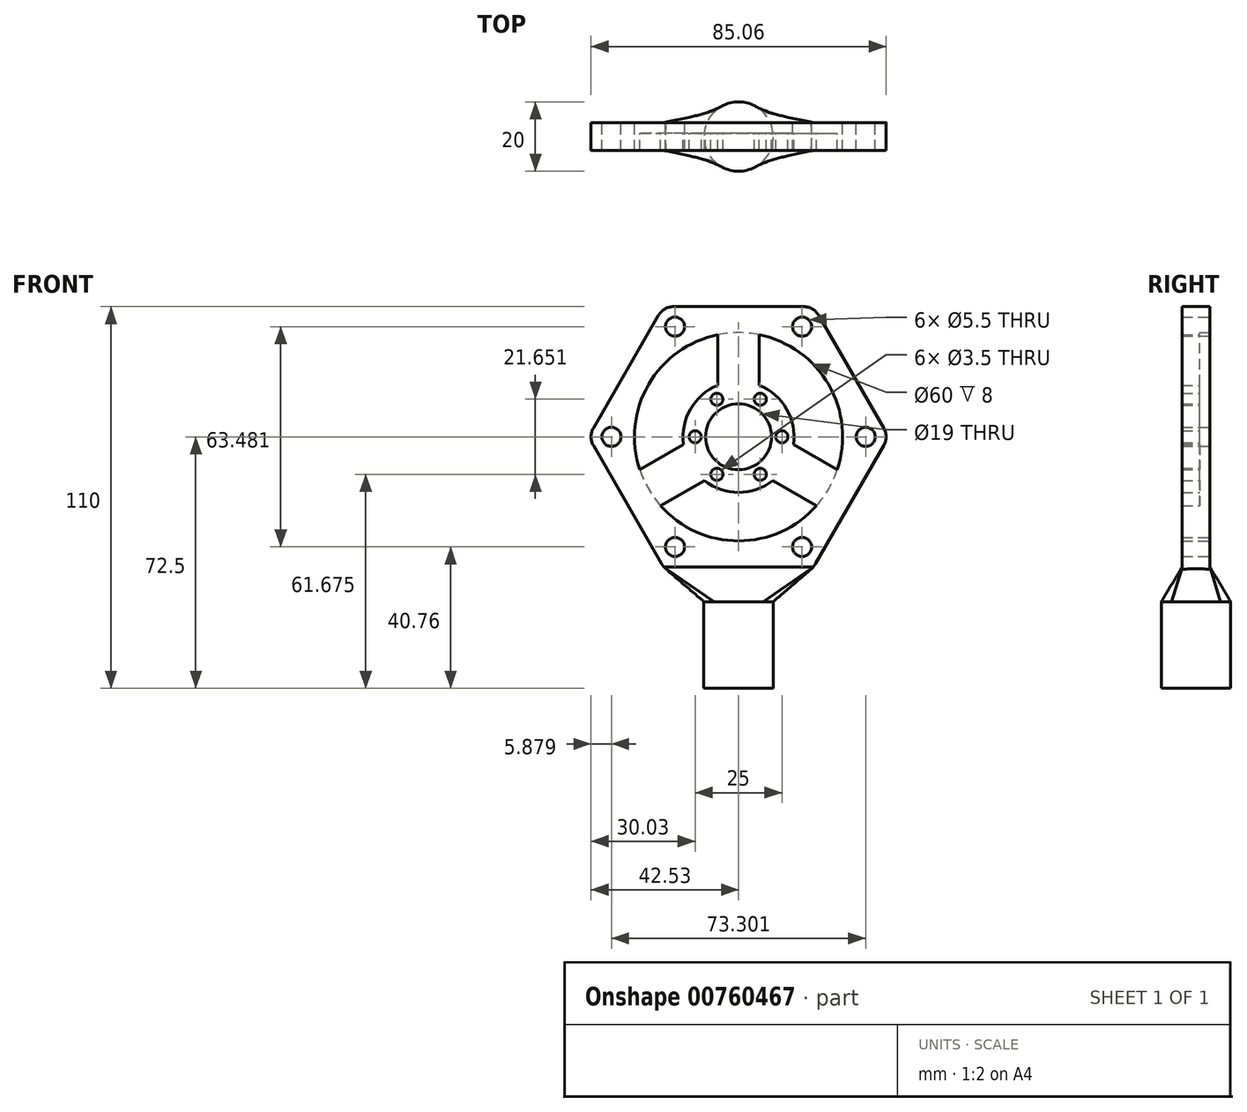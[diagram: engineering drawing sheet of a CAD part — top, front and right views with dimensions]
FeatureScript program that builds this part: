
annotation { "Feature Type Name" : "Feature", "Feature Type Description" : "" }
export const myFeature = defineFeature(function(context is Context, id is Id, definition is map)
    precondition{}
    {
        {
            var Q0;
            Q0=qCreatedBy(makeId("Front.planeOp"),FACE);
            var sketch = newSketch(context, id + "F0", { "sketchPlane" : qUnion([Q0])});
            skCircle(sketch, "E0.cCircle", {"center": v(0, 0) * mm, "radius": 37.5 * mm, "construction": true});
            skLineSegment(sketch, "E0.0", {"start": v(-21.65, 37.5) * mm, "end": v(21.65, 37.5) * mm});
            skLineSegment(sketch, "E0.1", {"start": v(21.65, 37.5) * mm, "end": v(43.3, 0) * mm});
            skLineSegment(sketch, "E0.2", {"start": v(43.3, 0) * mm, "end": v(21.65, -37.5) * mm});
            skLineSegment(sketch, "E0.3", {"start": v(21.65, -37.5) * mm, "end": v(-21.65, -37.5) * mm});
            skLineSegment(sketch, "E0.4", {"start": v(-21.65, -37.5) * mm, "end": v(-43.3, 0) * mm});
            skLineSegment(sketch, "E0.5", {"start": v(-43.3, 0) * mm, "end": v(-21.65, 37.5) * mm});
            skPoint(sketch, "E0.0.midPoint", {"position": v(0, 37.5) * mm});
            skCircle(sketch, "E1", {"center": v(0, 0) * mm, "radius": 30 * mm});
            skCircle(sketch, "E2", {"center": v(36.65, 0) * mm, "radius": 2.75 * mm});
            skLineSegment(sketch, "E3", {"start": v(43.3, 0) * mm, "end": v(30, 0) * mm});
            skCircle(sketch, "E4.1.0", {"center": v(18.33, 31.74) * mm, "radius": 2.75 * mm});
            skCircle(sketch, "E4.2.0", {"center": v(-18.33, 31.74) * mm, "radius": 2.75 * mm});
            skCircle(sketch, "E4.3.0", {"center": v(-36.65, 0) * mm, "radius": 2.75 * mm});
            skCircle(sketch, "E4.4.0", {"center": v(-18.33, -31.74) * mm, "radius": 2.75 * mm});
            skCircle(sketch, "E4.5.0", {"center": v(18.33, -31.74) * mm, "radius": 2.75 * mm});
            skCircle(sketch, "E5", {"center": v(0, 0) * mm, "radius": 16 * mm});
            skCircle(sketch, "E6", {"center": v(0, 0) * mm, "radius": 9.5 * mm});
            skCircle(sketch, "E7", {"center": v(-12.5, 0) * mm, "radius": 1.75 * mm});
            skCircle(sketch, "E8.1.0", {"center": v(-6.25, -10.83) * mm, "radius": 1.75 * mm});
            skCircle(sketch, "E8.2.0", {"center": v(6.25, -10.83) * mm, "radius": 1.75 * mm});
            skCircle(sketch, "E8.3.0", {"center": v(12.5, 0) * mm, "radius": 1.75 * mm});
            skCircle(sketch, "E8.4.0", {"center": v(6.25, 10.83) * mm, "radius": 1.75 * mm});
            skCircle(sketch, "E8.5.0", {"center": v(-6.25, 10.83) * mm, "radius": 1.75 * mm});
            skLineSegment(sketch, "E9", {"start": v(0, 16) * mm, "end": v(0, 30) * mm, "construction": true});
            skLineSegment(sketch, "E10", {"start": v(6, 14.83) * mm, "end": v(6, 29.4) * mm});
            skLineSegment(sketch, "E11.MirrorCS", {"start": v(-6, 14.83) * mm, "end": v(-6, 29.4) * mm});
            skLineSegment(sketch, "E12.1.0", {"start": v(-15.85, -2.22) * mm, "end": v(-28.46, -9.5) * mm});
            skLineSegment(sketch, "E12.1.1", {"start": v(-9.85, -12.61) * mm, "end": v(-22.46, -19.9) * mm});
            skLineSegment(sketch, "E12.2.0", {"start": v(9.85, -12.61) * mm, "end": v(22.46, -19.9) * mm});
            skLineSegment(sketch, "E12.2.1", {"start": v(15.85, -2.22) * mm, "end": v(28.46, -9.5) * mm});
            skSolve(sketch);
        }
        {
            var Q0;
            Q0=makeQuery(id+"F0.imprint","IMPRINT",FACE,{"disambiguationData":[TD([[makeQuery(id+"F0.imprint","IMPRINT",EDGE,{"derivedFrom":sQuery(id+"F0.wireOp",EDGE,"E0.0")}),-1.0]])]});
            extrude(context, id + "F1", {"entities" : qUnion([Q0]), "endBound" : BoundingType.SYMMETRIC, "depth" : 8 * mm, "offsetDistance" : 25 * mm});
        }
        {
            var Q0;
            Q0=makeQuery(id+"F1.opExtrude","SWEPT_FACE",FACE,{"disambiguationData":[OSD([sQuery(id+"F0.wireOp",EDGE,"E0.3")])]});
            cPlane(context, id + "F2", {"entities" : qUnion([Q0]), "cplaneType" : CPlaneType.OFFSET, "offset" : 10 * mm, "width" : 150 * mm, "height" : 150 * mm});
        }
        {
            var Q0;
            Q0=qCreatedBy(id+"F2.planeOp",FACE);
            var sketch = newSketch(context, id + "F3", { "sketchPlane" : qUnion([Q0])});
            skLineSegment(sketch, "E13.bottom", {"start": v(7.07, 7.07) * mm, "end": v(-7.07, 7.07) * mm, "construction": true});
            skLineSegment(sketch, "E13.top", {"start": v(7.07, -7.07) * mm, "end": v(-7.07, -7.07) * mm, "construction": true});
            skLineSegment(sketch, "E13.left", {"start": v(7.07, 7.07) * mm, "end": v(7.07, -7.07) * mm, "construction": true});
            skLineSegment(sketch, "E13.right", {"start": v(-7.07, 7.07) * mm, "end": v(-7.07, -7.07) * mm, "construction": true});
            skPoint(sketch, "E13.middle", {"position": v(0, 0) * mm});
            skCircle(sketch, "E14", {"center": v(0, 0) * mm, "radius": 10 * mm});
            skSolve(sketch);
        }
        {
            var Q0;
            Q0=sQuery(id+"FgavMsP0AKGjl20_1.wireOp",EDGE,"DRp4sTKl-kvSm-M3R3-zUVl-CTIJX1aC9KoG");
            var Q2;
            Q2=makeQuery(id+"F3.imprint","IMPRINT",FACE,{"disambiguationData":[TD([[makeQuery(id+"F3.imprint","IMPRINT",EDGE,{"derivedFrom":sQuery(id+"F3.wireOp",EDGE,"E14")}),1.0]])]});
            var Q3;
            Q3=makeQuery(id+"F1.opExtrude","SWEPT_FACE",FACE,{"disambiguationData":[OSD([sQuery(id+"F0.wireOp",EDGE,"E0.3")])]});
            var Q4;
            Q4=makeQuery(id+"F1.opExtrude","CAP_VERTEX",VERTEX,{"disambiguationData":[OSD([sQuery(id+"F0.wireOp",EDGE,"E0.2"),sQuery(id+"F0.wireOp",EDGE,"E0.3")])],"isStart":false});
            var Q5;
            Q5=sQuery(id+"F3.wireOp",VERTEX,"E13.bottom.start");
            loft(context, id + "F4", {"operationType" : NewBodyOperationType.ADD, "spine" : qUnion([Q0]), "sheetProfilesArray" : [{ "sheetProfileEntities" : qUnion([Q2]) }, { "sheetProfileEntities" : qUnion([Q3]) }], "matchConnections" : true, "connections" : [{ "connectionEntities" : qUnion([Q4, Q5]), "connectionEdgeQueries" : qUnion([]), "connectionEdgeParameters" : [] }]});
        }
        {
            var Q0;
            Q0=makeQuery(id+"F4.opLoft","CAP_FACE",FACE,{"disambiguationData":[OSD([makeQuery(id+"F3.imprint","IMPRINT",FACE,{"disambiguationData":[TD([[makeQuery(id+"F3.imprint","IMPRINT",EDGE,{"derivedFrom":sQuery(id+"F3.wireOp",EDGE,"E14")}),1.0]])]})])],"isStart":true});
            extrude(context, id + "F5", {"entities" : qUnion([Q0]), "operationType" : NewBodyOperationType.ADD, "depth" : 25 * mm, "offsetDistance" : 25 * mm});
        }
        {
            var Q0;
            Q0=makeQuery(id+"F0.imprint","IMPRINT",FACE,{"disambiguationData":[TD([[makeQuery(id+"F0.imprint","IMPRINT",EDGE,{"derivedFrom":sQuery(id+"F0.wireOp",EDGE,"E6")}),-1.0]])]});
            var Q1;
            {var subQ0=sQuery(id+"F0.wireOp",EDGE,"E10");Q1=makeQuery(id+"F0.imprint","IMPRINT",FACE,{"disambiguationData":[TD([[makeQuery(id+"F0.imprint","IMPRINT",EDGE,{"derivedFrom":subQ0}),1.0]])]});}
            var Q2;
            {var subQ0=sQuery(id+"F0.wireOp",EDGE,"E12.1.0");Q2=makeQuery(id+"F0.imprint","IMPRINT",FACE,{"disambiguationData":[TD([[makeQuery(id+"F0.imprint","IMPRINT",EDGE,{"derivedFrom":subQ0}),1.0]])]});}
            var Q3;
            {var subQ0=sQuery(id+"F0.wireOp",EDGE,"E12.2.0");Q3=makeQuery(id+"F0.imprint","IMPRINT",FACE,{"disambiguationData":[TD([[makeQuery(id+"F0.imprint","IMPRINT",EDGE,{"derivedFrom":subQ0}),1.0]])]});}
            extrude(context, id + "F6", {"entities" : qUnion([Q0, Q1, Q2, Q3]), "operationType" : NewBodyOperationType.ADD, "depth" : 4 * mm, "offsetDistance" : 25 * mm, "hasSecondDirection" : true, "secondDirectionOppositeDirection" : true, "secondDirectionDepth" : 1 * mm});
        }
        {
            var Q0;
            Q0=makeQuery(id+"F1.opExtrude","SWEPT_EDGE",EDGE,{"disambiguationData":[OSD([sQuery(id+"F0.wireOp",EDGE,"E0.0"),sQuery(id+"F0.wireOp",EDGE,"E0.5")])]});
            var Q1;
            Q1=makeQuery(id+"F1.opExtrude","SWEPT_EDGE",EDGE,{"disambiguationData":[OSD([sQuery(id+"F0.wireOp",EDGE,"E0.0"),sQuery(id+"F0.wireOp",EDGE,"E0.1")])]});
            var Q2;
            Q2=makeQuery(id+"F1.opExtrude","SWEPT_EDGE",EDGE,{"disambiguationData":[OSD([sQuery(id+"F0.wireOp",EDGE,"E0.4"),sQuery(id+"F0.wireOp",EDGE,"E0.5")])]});
            var Q3;
            Q3=makeQuery(id+"F1.opExtrude","SWEPT_EDGE",EDGE,{"disambiguationData":[OSD([sQuery(id+"F0.wireOp",EDGE,"E0.1"),sQuery(id+"F0.wireOp",EDGE,"E0.2")])]});
            var Q4;
            {var subQ0=sQuery(id+"F0.wireOp",EDGE,"E0.4");var subQ1=sQuery(id+"F0.wireOp",EDGE,"E0.3");Q4=makeQuery(id+"F4.boolean.opBoolean","MERGE",EDGE,{"derivedFrom":[makeQuery(id+"F1.opExtrude","SWEPT_EDGE",EDGE,{"disambiguationData":[OSD([subQ1,subQ0])]}),makeQuery(id+"F4.opLoft","MID_CAP_EDGE",EDGE,{"disambiguationData":[OSD([subQ1,subQ0])],"capPos":1.0})]});}
            var Q5;
            {var subQ0=sQuery(id+"F0.wireOp",EDGE,"E0.3");var subQ1=sQuery(id+"F0.wireOp",EDGE,"E0.2");Q5=makeQuery(id+"F4.boolean.opBoolean","MERGE",EDGE,{"derivedFrom":[makeQuery(id+"F1.opExtrude","SWEPT_EDGE",EDGE,{"disambiguationData":[OSD([subQ1,subQ0])]}),makeQuery(id+"F4.opLoft","MID_CAP_EDGE",EDGE,{"disambiguationData":[OSD([subQ1,subQ0])],"capPos":1.0})]});}
            var Q6;
            {var subQ0=sQuery(id+"F0.wireOp",EDGE,"E1");Q6=makeQuery(id+"F6.opExtrude","CAP_EDGE",EDGE,{"disambiguationData":[OSD([subQ0]),TDD([makeQuery(id+"F0.imprint","IMPRINT",EDGE,{"disambiguationData":[TD([[makeQuery(id+"F0.imprint","INTERSECT",VERTEX,{"derivedFrom":[subQ0,sQuery(id+"F0.wireOp",EDGE,"E12.1.0")]}),-1.0]])],"derivedFrom":subQ0})])],"isStart":true});}
            var Q7;
            {var subQ0=sQuery(id+"F0.wireOp",EDGE,"E1");Q7=makeQuery(id+"F6.opExtrude","CAP_EDGE",EDGE,{"disambiguationData":[OSD([subQ0]),TDD([makeQuery(id+"F0.imprint","IMPRINT",EDGE,{"disambiguationData":[TD([[makeQuery(id+"F0.imprint","INTERSECT",VERTEX,{"derivedFrom":[subQ0,sQuery(id+"F0.wireOp",EDGE,"E12.2.0")]}),-1.0]])],"derivedFrom":subQ0})])],"isStart":true});}
            var Q8;
            {var subQ0=sQuery(id+"F0.wireOp",EDGE,"E1");Q8=makeQuery(id+"F6.opExtrude","CAP_EDGE",EDGE,{"disambiguationData":[OSD([subQ0]),TDD([makeQuery(id+"F0.imprint","IMPRINT",EDGE,{"disambiguationData":[TD([[makeQuery(id+"F0.imprint","INTERSECT",VERTEX,{"derivedFrom":[subQ0,sQuery(id+"F0.wireOp",EDGE,"E10")]}),-1.0]])],"derivedFrom":subQ0})])],"isStart":true});}
            var Q9;
            {var subQ0=sQuery(id+"F0.wireOp",EDGE,"E1");Q9=makeQuery(id+"F6.opExtrude","CAP_EDGE",EDGE,{"disambiguationData":[OSD([subQ0]),TDD([makeQuery(id+"F0.imprint","IMPRINT",EDGE,{"disambiguationData":[TD([[makeQuery(id+"F0.imprint","INTERSECT",VERTEX,{"derivedFrom":[subQ0,sQuery(id+"F0.wireOp",EDGE,"E12.1.0")]}),-1.0]])],"derivedFrom":subQ0})])],"isStart":false});}
            var Q10;
            {var subQ0=sQuery(id+"F0.wireOp",EDGE,"E1");Q10=makeQuery(id+"F6.opExtrude","CAP_EDGE",EDGE,{"disambiguationData":[OSD([subQ0]),TDD([makeQuery(id+"F0.imprint","IMPRINT",EDGE,{"disambiguationData":[TD([[makeQuery(id+"F0.imprint","INTERSECT",VERTEX,{"derivedFrom":[subQ0,sQuery(id+"F0.wireOp",EDGE,"E10")]}),-1.0]])],"derivedFrom":subQ0})])],"isStart":false});}
            var Q11;
            {var subQ0=sQuery(id+"F0.wireOp",EDGE,"E1");Q11=makeQuery(id+"F6.opExtrude","CAP_EDGE",EDGE,{"disambiguationData":[OSD([subQ0]),TDD([makeQuery(id+"F0.imprint","IMPRINT",EDGE,{"disambiguationData":[TD([[makeQuery(id+"F0.imprint","INTERSECT",VERTEX,{"derivedFrom":[subQ0,sQuery(id+"F0.wireOp",EDGE,"E12.2.0")]}),-1.0]])],"derivedFrom":subQ0})])],"isStart":false});}
            fillet(context, id + "F7", {"entities" : qUnion([Q0, Q1, Q2, Q3, Q4, Q5, Q6, Q7, Q8, Q9, Q10, Q11]), "radius" : 5 * mm, "tangentPropagation" : true, "allowEdgeOverflow" : false});
        }
    });
